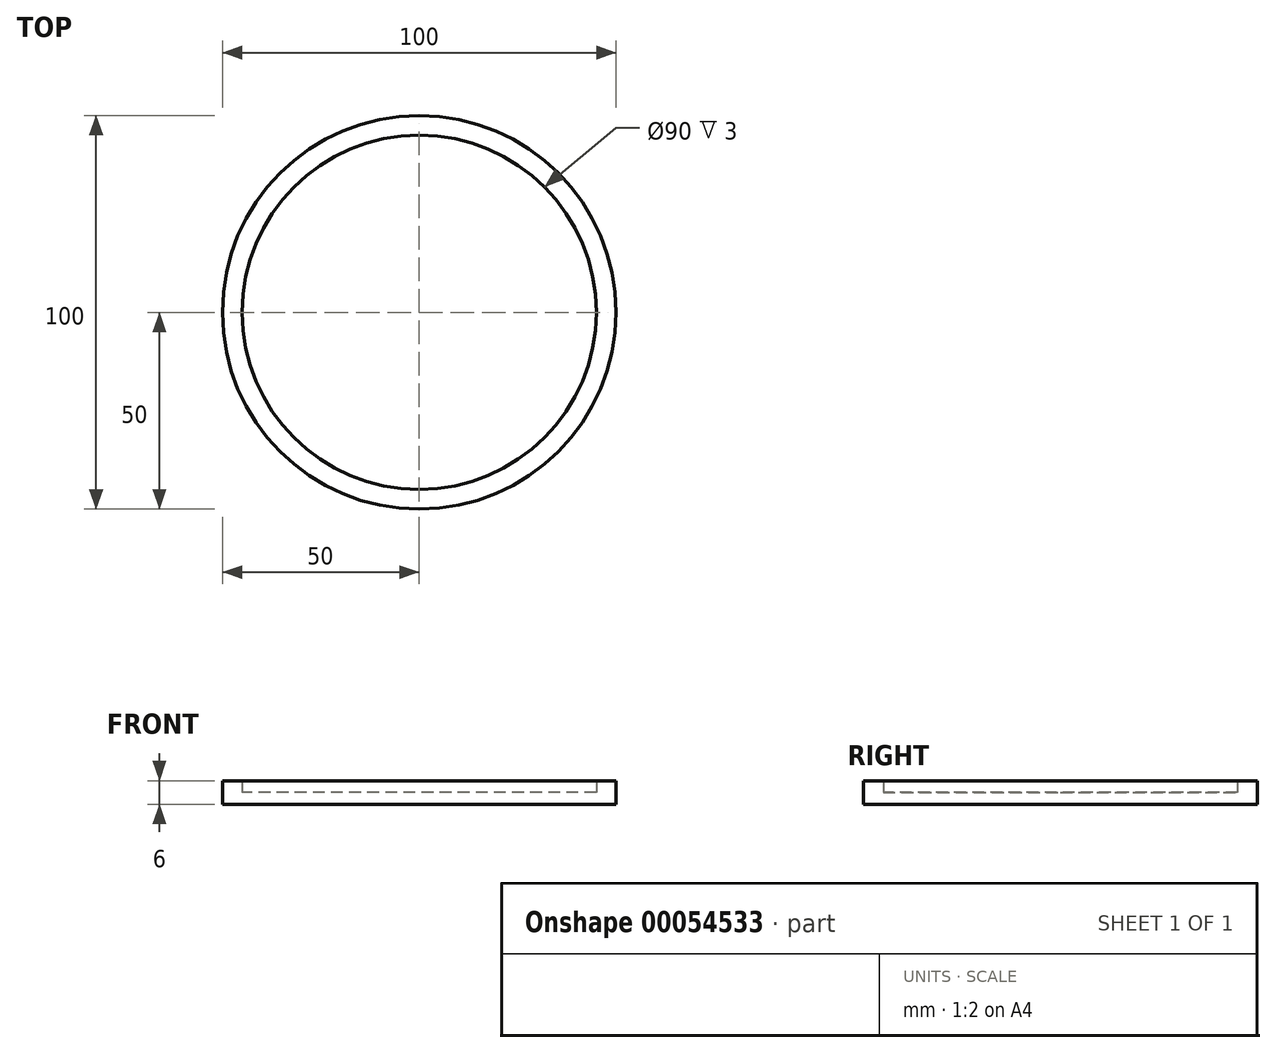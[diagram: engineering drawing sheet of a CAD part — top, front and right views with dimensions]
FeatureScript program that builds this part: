
annotation { "Feature Type Name" : "Feature", "Feature Type Description" : "" }
export const myFeature = defineFeature(function(context is Context, id is Id, definition is map)
    precondition{}
    {
        {
            assignVariable(context, id + "F0", {"name" : "defaultThickness", "anyValue" : 3});
        }
        {
            var Q0;
            Q0=qCreatedBy(makeId("Top.planeOp"),FACE);
            var sketch = newSketch(context, id + "F1", { "sketchPlane" : qUnion([Q0])});
            skCircle(sketch, "E0", {"center": v(0, 0) * mm, "radius": 50 * mm});
            skSolve(sketch);
        }
        {
            var Q0;
            Q0=makeQuery(id+"F1.imprint","IMPRINT",FACE,{"disambiguationData":[TD([[makeQuery(id+"F1.imprint","IMPRINT",EDGE,{"derivedFrom":sQuery(id+"F1.wireOp",EDGE,"E0")}),1.0]])]});
            extrude(context, id + "F2", {"entities" : qUnion([Q0]), "depth" : (getVariable(context, 'defaultThickness')) * mm});
        }
        {
            var Q0;
            Q0=makeQuery(id+"F2.opExtrude","CAP_FACE",FACE,{"disambiguationData":[OSD([sQuery(id+"F1.wireOp",EDGE,"E0")])],"isStart":false});
            var sketch = newSketch(context, id + "F3", { "sketchPlane" : qUnion([Q0])});
            skCircle(sketch, "E1", {"center": v(0, 0) * mm, "radius": 45 * mm});
            skSolve(sketch);
        }
        {
            var Q0;
            Q0=makeQuery(id+"F3.imprint","IMPRINT",FACE,{"disambiguationData":[TD([[makeQuery(id+"F3.imprint","IMPRINT",EDGE,{"derivedFrom":sQuery(id+"F3.wireOp",EDGE,"E1")}),-1.0]])]});
            extrude(context, id + "F4", {"entities" : qUnion([Q0]), "operationType" : NewBodyOperationType.ADD, "depth" : (getVariable(context, 'defaultThickness')) * mm});
        }
    });
